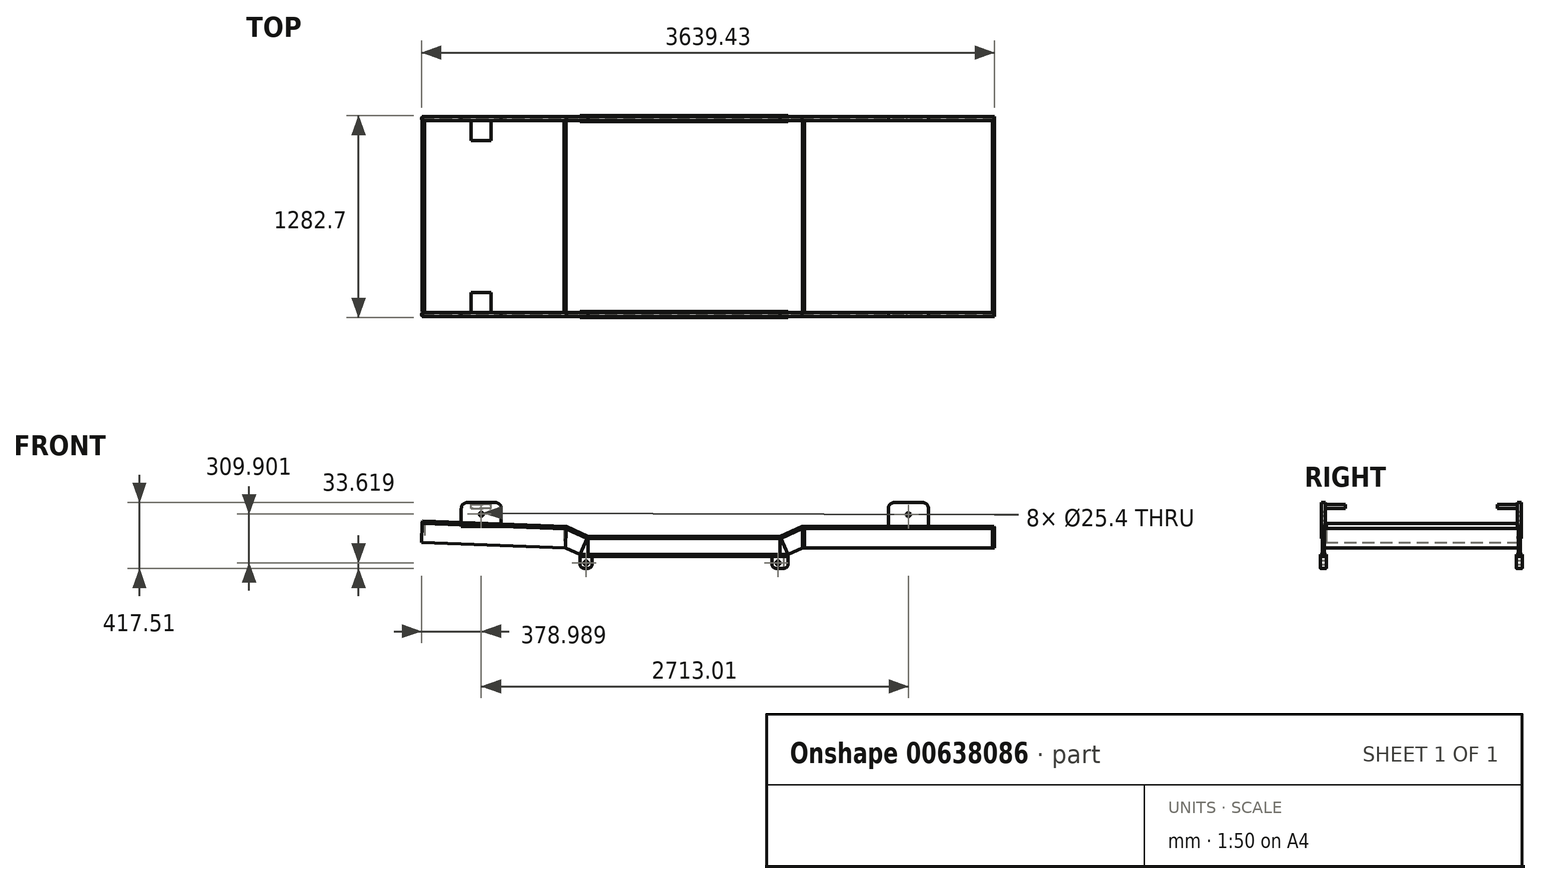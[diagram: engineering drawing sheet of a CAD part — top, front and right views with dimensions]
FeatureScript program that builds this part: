
annotation { "Feature Type Name" : "Feature", "Feature Type Description" : "" }
export const myFeature = defineFeature(function(context is Context, id is Id, definition is map)
    precondition{}
    {
        {
            var Q0;
            Q0=qCreatedBy(makeId("Right.planeOp"),FACE);
            var sketch = newSketch(context, id + "F0", { "sketchPlane" : qUnion([Q0])});
            skLineSegment(sketch, "E0.bottom", {"start": v(-635, 0) * mm, "end": v(-609.6, 0) * mm});
            skLineSegment(sketch, "E0.top", {"start": v(-635, -12.7) * mm, "end": v(-609.6, -12.7) * mm});
            skLineSegment(sketch, "E0.left", {"start": v(-635, 0) * mm, "end": v(-635, -12.7) * mm});
            skLineSegment(sketch, "E0.right", {"start": v(-609.6, 0) * mm, "end": v(-609.6, -12.7) * mm});
            skLineSegment(sketch, "E1.bottom", {"start": v(-628.65, -12.7) * mm, "end": v(-615.95, -12.7) * mm});
            skLineSegment(sketch, "E1.top", {"start": v(-628.65, -114.3) * mm, "end": v(-615.95, -114.3) * mm});
            skLineSegment(sketch, "E1.left", {"start": v(-628.65, -12.7) * mm, "end": v(-628.65, -114.3) * mm});
            skLineSegment(sketch, "E1.right", {"start": v(-615.95, -12.7) * mm, "end": v(-615.95, -114.3) * mm});
            skLineSegment(sketch, "E2.bottom", {"start": v(-641.35, -114.3) * mm, "end": v(-603.25, -114.3) * mm});
            skLineSegment(sketch, "E2.top", {"start": v(-641.35, -127) * mm, "end": v(-603.25, -127) * mm});
            skLineSegment(sketch, "E2.left", {"start": v(-641.35, -114.3) * mm, "end": v(-641.35, -127) * mm});
            skLineSegment(sketch, "E2.right", {"start": v(-603.25, -114.3) * mm, "end": v(-603.25, -127) * mm});
            skLineSegment(sketch, "E3", {"start": v(0, 0) * mm, "end": v(0, -132.95) * mm});
            skLineSegment(sketch, "E4.MirrorCS", {"start": v(635, 0) * mm, "end": v(609.6, 0) * mm});
            skLineSegment(sketch, "E5.MirrorCS", {"start": v(635, 0) * mm, "end": v(635, -12.7) * mm});
            skLineSegment(sketch, "E6.MirrorCS", {"start": v(628.65, -12.7) * mm, "end": v(615.95, -12.7) * mm});
            skLineSegment(sketch, "E7.MirrorCS", {"start": v(635, -12.7) * mm, "end": v(609.6, -12.7) * mm});
            skLineSegment(sketch, "E8.MirrorCS", {"start": v(609.6, 0) * mm, "end": v(609.6, -12.7) * mm});
            skLineSegment(sketch, "E9.MirrorCS", {"start": v(615.95, -12.7) * mm, "end": v(615.95, -114.3) * mm});
            skLineSegment(sketch, "E10.MirrorCS", {"start": v(628.65, -12.7) * mm, "end": v(628.65, -114.3) * mm});
            skLineSegment(sketch, "E11.MirrorCS", {"start": v(641.35, -127) * mm, "end": v(603.25, -127) * mm});
            skLineSegment(sketch, "E12.MirrorCS", {"start": v(603.25, -114.3) * mm, "end": v(603.25, -127) * mm});
            skLineSegment(sketch, "E13.MirrorCS", {"start": v(641.35, -114.3) * mm, "end": v(641.35, -127) * mm});
            skLineSegment(sketch, "E14.MirrorCS", {"start": v(641.35, -114.3) * mm, "end": v(603.25, -114.3) * mm});
            skLineSegment(sketch, "E15", {"start": v(-609.6, -12.7) * mm, "end": v(609.6, -12.7) * mm});
            skLineSegment(sketch, "E16.bottom", {"start": v(615.95, -12.7) * mm, "end": v(628.65, -12.7) * mm});
            skLineSegment(sketch, "E16.top", {"start": v(615.95, -114.3) * mm, "end": v(628.65, -114.3) * mm});
            skSolve(sketch);
        }
        {
            var Q0;
            Q0=makeQuery(id+"F0.imprint","IMPRINT",FACE,{"disambiguationData":[TD([[makeQuery(id+"F0.imprint","IMPRINT",EDGE,{"derivedFrom":sQuery(id+"F0.wireOp",EDGE,"E6.MirrorCS")}),1.0]])]});
            var Q1;
            Q1=makeQuery(id+"F0.imprint","IMPRINT",FACE,{"disambiguationData":[TD([[makeQuery(id+"F0.imprint","IMPRINT",EDGE,{"derivedFrom":sQuery(id+"F0.wireOp",EDGE,"E4.MirrorCS")}),1.0]])]});
            var Q2;
            Q2=makeQuery(id+"F0.imprint","IMPRINT",FACE,{"disambiguationData":[TD([[makeQuery(id+"F0.imprint","IMPRINT",EDGE,{"derivedFrom":sQuery(id+"F0.wireOp",EDGE,"E11.MirrorCS")}),-1.0]])]});
            var Q3;
            Q3=makeQuery(id+"F0.imprint","IMPRINT",FACE,{"disambiguationData":[TD([[makeQuery(id+"F0.imprint","IMPRINT",EDGE,{"derivedFrom":sQuery(id+"F0.wireOp",EDGE,"E1.top")}),1.0]])]});
            var Q4;
            Q4=makeQuery(id+"F0.imprint","IMPRINT",FACE,{"disambiguationData":[TD([[makeQuery(id+"F0.imprint","IMPRINT",EDGE,{"derivedFrom":sQuery(id+"F0.wireOp",EDGE,"E0.bottom")}),-1.0]])]});
            var Q5;
            Q5=makeQuery(id+"F0.imprint","IMPRINT",FACE,{"disambiguationData":[TD([[makeQuery(id+"F0.imprint","IMPRINT",EDGE,{"derivedFrom":sQuery(id+"F0.wireOp",EDGE,"E2.bottom")}),-1.0]])]});
            extrude(context, id + "F1", {"entities" : qUnion([Q0, Q1, Q2, Q3, Q4, Q5]), "depth" : 1219.2 * mm, "offsetDistance" : 25.4 * mm});
        }
        {
            var Q0;
            Q0=makeQuery(id+"F1.opExtrude","CAP_FACE",FACE,{"disambiguationData":[OSD([sQuery(id+"F0.wireOp",EDGE,"E4.MirrorCS"),sQuery(id+"F0.wireOp",EDGE,"E5.MirrorCS"),sQuery(id+"F0.wireOp",EDGE,"E7.MirrorCS"),sQuery(id+"F0.wireOp",EDGE,"E8.MirrorCS"),sQuery(id+"F0.wireOp",EDGE,"E9.MirrorCS"),sQuery(id+"F0.wireOp",EDGE,"E10.MirrorCS"),sQuery(id+"F0.wireOp",EDGE,"E16.top")])],"isStart":true});
            var sketch = newSketch(context, id + "F2", { "sketchPlane" : qUnion([Q0])});
            skLineSegment(sketch, "E17.bottom", {"start": v(-628.65, -12.7) * mm, "end": v(-615.95, -12.7) * mm});
            skLineSegment(sketch, "E17.top", {"start": v(-628.65, -114.3) * mm, "end": v(-615.95, -114.3) * mm});
            skLineSegment(sketch, "E17.left", {"start": v(-628.65, -12.7) * mm, "end": v(-628.65, -114.3) * mm});
            skLineSegment(sketch, "E17.right", {"start": v(-615.95, -12.7) * mm, "end": v(-615.95, -114.3) * mm});
            skLineSegment(sketch, "E18.bottom", {"start": v(-635, 0) * mm, "end": v(-609.6, 0) * mm});
            skLineSegment(sketch, "E18.top", {"start": v(-635, -12.7) * mm, "end": v(-609.6, -12.7) * mm});
            skLineSegment(sketch, "E18.left", {"start": v(-635, 0) * mm, "end": v(-635, -12.7) * mm});
            skLineSegment(sketch, "E18.right", {"start": v(-609.6, 0) * mm, "end": v(-609.6, -12.7) * mm});
            skLineSegment(sketch, "E19.bottom", {"start": v(-641.35, -114.34) * mm, "end": v(-603.26, -114.34) * mm});
            skLineSegment(sketch, "E19.top", {"start": v(-641.35, -127.04) * mm, "end": v(-603.26, -127.04) * mm});
            skLineSegment(sketch, "E19.left", {"start": v(-641.35, -114.34) * mm, "end": v(-641.35, -127.04) * mm});
            skLineSegment(sketch, "E19.right", {"start": v(-603.26, -114.34) * mm, "end": v(-603.26, -127.04) * mm});
            skLineSegment(sketch, "E20", {"start": v(0, 80.16) * mm, "end": v(0, -74.98) * mm});
            skLineSegment(sketch, "E21", {"start": v(0, 80.16) * mm, "end": v(0, -337.85) * mm});
            skLineSegment(sketch, "E22.MirrorCS", {"start": v(635, 0) * mm, "end": v(609.6, 0) * mm});
            skLineSegment(sketch, "E23.MirrorCS", {"start": v(609.6, 0) * mm, "end": v(609.6, -12.7) * mm});
            skLineSegment(sketch, "E24.MirrorCS", {"start": v(635, 0) * mm, "end": v(635, -12.7) * mm});
            skLineSegment(sketch, "E25.MirrorCS", {"start": v(615.95, -12.7) * mm, "end": v(615.95, -114.3) * mm});
            skLineSegment(sketch, "E26.MirrorCS", {"start": v(628.65, -12.7) * mm, "end": v(628.65, -114.3) * mm});
            skLineSegment(sketch, "E27.MirrorCS", {"start": v(603.26, -114.34) * mm, "end": v(603.26, -127.04) * mm});
            skLineSegment(sketch, "E28.MirrorCS", {"start": v(641.35, -127.04) * mm, "end": v(603.26, -127.04) * mm});
            skLineSegment(sketch, "E29.MirrorCS", {"start": v(641.35, -114.34) * mm, "end": v(641.35, -127.04) * mm});
            skSolve(sketch);
        }
        {
            var Q0;
            {var subQ2=sQuery(id+"F2.wireOp",EDGE,"E17.bottom");var subQ6=makeQuery(id+"F2.imprint","IMPRINT",EDGE,{"derivedFrom":subQ2});Q0=qUnion([makeQuery(id+"F2.imprint","IMPRINT",FACE,{"disambiguationData":[TD([[makeQuery(id+"F2.imprint","IMPRINT",EDGE,{"derivedFrom":sQuery(id+"F2.wireOp",EDGE,"E19.bottom")}),-1.0]])]}),makeQuery(id+"F2.imprint","IMPRINT",FACE,{"disambiguationData":[TD([[subQ6,-1.0]])]}),makeQuery(id+"F2.imprint","IMPRINT",FACE,{"disambiguationData":[TD([[subQ6,1.0]])]})]);}
            var Q1;
            Q1=makeQuery(id+"F1.opExtrude","CAP_FACE",FACE,{"disambiguationData":[OSD([sQuery(id+"F0.wireOp",EDGE,"E0.bottom"),sQuery(id+"F0.wireOp",EDGE,"E0.top"),sQuery(id+"F0.wireOp",EDGE,"E0.left"),sQuery(id+"F0.wireOp",EDGE,"E0.right"),sQuery(id+"F0.wireOp",EDGE,"E1.top"),sQuery(id+"F0.wireOp",EDGE,"E1.left"),sQuery(id+"F0.wireOp",EDGE,"E1.right")])],"isStart":true});
            extrude(context, id + "F3", {"entities" : qUnion([Q0, Q1]), "depth" : 50.8 * mm, "offsetDistance" : 25.4 * mm});
        }
        {
            var Q0;
            Q0=makeQuery(id+"F1.opExtrude","CAP_FACE",FACE,{"disambiguationData":[OSD([sQuery(id+"F0.wireOp",EDGE,"E2.bottom"),sQuery(id+"F0.wireOp",EDGE,"E2.top"),sQuery(id+"F0.wireOp",EDGE,"E2.left"),sQuery(id+"F0.wireOp",EDGE,"E2.right")])],"isStart":true});
            extrude(context, id + "F4", {"entities" : qUnion([Q0]), "operationType" : NewBodyOperationType.ADD, "depth" : 50.8 * mm, "offsetDistance" : 25.4 * mm});
        }
        {
            var Q0;
            Q0=makeQuery(id+"F3.opExtrude","CAP_EDGE",EDGE,{"disambiguationData":[OSD([sQuery(id+"F0.wireOp",EDGE,"E0.bottom")])],"isStart":false});
            chamfer(context, id + "F5", {"entities" : qUnion([Q0]), "chamferType" : ChamferType.TWO_OFFSETS, "width1" : 114.3 * mm, "oppositeDirection" : false, "width2" : 50.8 * mm, "tangentPropagation" : true});
        }
        {
            var Q0;
            Q0=makeQuery(id+"F3.opExtrude","CAP_EDGE",EDGE,{"disambiguationData":[OSD([sQuery(id+"F2.wireOp",EDGE,"E18.bottom")])],"isStart":false});
            chamfer(context, id + "F6", {"entities" : qUnion([Q0]), "chamferType" : ChamferType.TWO_OFFSETS, "width1" : 50.8 * mm, "oppositeDirection" : false, "width2" : 114.3 * mm, "tangentPropagation" : true});
        }
        {
            var Q0;
            Q0=makeQuery(id+"F6.opChamfer","BLEND_FACE",FACE,{"disambiguationData":[OSD([sQuery(id+"F2.wireOp",EDGE,"E18.bottom")])]});
            var Q1;
            Q1=makeQuery(id+"F5.opChamfer","BLEND_FACE",FACE,{"disambiguationData":[OSD([sQuery(id+"F0.wireOp",EDGE,"E0.bottom")])]});
            extrude(context, id + "F7", {"entities" : qUnion([Q0, Q1]), "depth" : 152.4 * mm, "offsetDistance" : 25.4 * mm});
        }
        {
            var Q0;
            Q0=makeQuery(id+"F7.opExtrude","CAP_EDGE",EDGE,{"disambiguationData":[OSD([sQuery(id+"F2.wireOp",EDGE,"E17.top"),sQuery(id+"F2.wireOp",EDGE,"E18.bottom")])],"isStart":false});
            chamfer(context, id + "F8", {"entities" : qUnion([Q0]), "chamferType" : ChamferType.TWO_OFFSETS, "width1" : 50.8 * mm, "oppositeDirection" : false, "width2" : 127 * mm, "tangentPropagation" : true});
        }
        {
            var Q0;
            Q0=makeQuery(id+"F7.opExtrude","CAP_EDGE",EDGE,{"disambiguationData":[OSD([sQuery(id+"F0.wireOp",EDGE,"E0.bottom"),sQuery(id+"F0.wireOp",EDGE,"E1.top")])],"isStart":false});
            chamfer(context, id + "F9", {"entities" : qUnion([Q0]), "chamferType" : ChamferType.TWO_OFFSETS, "width1" : 50.8 * mm, "oppositeDirection" : false, "width2" : 127 * mm, "tangentPropagation" : true});
        }
        {
            var Q0;
            Q0=makeQuery(id+"F8.opChamfer","BLEND_FACE",FACE,{"disambiguationData":[OSD([sQuery(id+"F2.wireOp",EDGE,"E17.top"),sQuery(id+"F2.wireOp",EDGE,"E18.bottom")])]});
            var Q1;
            Q1=makeQuery(id+"F9.opChamfer","BLEND_FACE",FACE,{"disambiguationData":[OSD([sQuery(id+"F0.wireOp",EDGE,"E0.bottom"),sQuery(id+"F0.wireOp",EDGE,"E1.top")])]});
            extrude(context, id + "F10", {"entities" : qUnion([Q0, Q1]), "depth" : 914.4 * mm, "offsetDistance" : 25.4 * mm});
        }
        {
            var Q0;
            Q0=makeQuery(id+"F1.opExtrude","CAP_FACE",FACE,{"disambiguationData":[OSD([sQuery(id+"F0.wireOp",EDGE,"E0.bottom"),sQuery(id+"F0.wireOp",EDGE,"E0.top"),sQuery(id+"F0.wireOp",EDGE,"E0.left"),sQuery(id+"F0.wireOp",EDGE,"E0.right"),sQuery(id+"F0.wireOp",EDGE,"E1.top"),sQuery(id+"F0.wireOp",EDGE,"E1.left"),sQuery(id+"F0.wireOp",EDGE,"E1.right")])],"isStart":false});
            var Q1;
            Q1=makeQuery(id+"F1.opExtrude","CAP_FACE",FACE,{"disambiguationData":[OSD([sQuery(id+"F0.wireOp",EDGE,"E2.bottom"),sQuery(id+"F0.wireOp",EDGE,"E2.top"),sQuery(id+"F0.wireOp",EDGE,"E2.left"),sQuery(id+"F0.wireOp",EDGE,"E2.right")])],"isStart":false});
            var Q2;
            Q2=makeQuery(id+"F1.opExtrude","CAP_FACE",FACE,{"disambiguationData":[OSD([sQuery(id+"F0.wireOp",EDGE,"E4.MirrorCS"),sQuery(id+"F0.wireOp",EDGE,"E5.MirrorCS"),sQuery(id+"F0.wireOp",EDGE,"E7.MirrorCS"),sQuery(id+"F0.wireOp",EDGE,"E8.MirrorCS"),sQuery(id+"F0.wireOp",EDGE,"E9.MirrorCS"),sQuery(id+"F0.wireOp",EDGE,"E10.MirrorCS"),sQuery(id+"F0.wireOp",EDGE,"E16.top")])],"isStart":false});
            var Q3;
            Q3=makeQuery(id+"F1.opExtrude","CAP_FACE",FACE,{"disambiguationData":[OSD([sQuery(id+"F0.wireOp",EDGE,"E11.MirrorCS"),sQuery(id+"F0.wireOp",EDGE,"E12.MirrorCS"),sQuery(id+"F0.wireOp",EDGE,"E13.MirrorCS"),sQuery(id+"F0.wireOp",EDGE,"E14.MirrorCS")])],"isStart":false});
            extrude(context, id + "F11", {"entities" : qUnion([Q0, Q1, Q2, Q3]), "depth" : 50.8 * mm, "offsetDistance" : 25.4 * mm});
        }
        {
            var Q0;
            Q0=makeQuery(id+"F11.opExtrude","CAP_EDGE",EDGE,{"disambiguationData":[OSD([sQuery(id+"F0.wireOp",EDGE,"E0.bottom")])],"isStart":false});
            chamfer(context, id + "F12", {"entities" : qUnion([Q0]), "chamferType" : ChamferType.TWO_OFFSETS, "width1" : 50.8 * mm, "oppositeDirection" : false, "width2" : 114.3 * mm, "tangentPropagation" : true});
        }
        {
            var Q0;
            Q0=makeQuery(id+"F11.opExtrude","CAP_EDGE",EDGE,{"disambiguationData":[OSD([sQuery(id+"F0.wireOp",EDGE,"E4.MirrorCS")])],"isStart":false});
            chamfer(context, id + "F13", {"entities" : qUnion([Q0]), "chamferType" : ChamferType.TWO_OFFSETS, "width1" : 114.3 * mm, "oppositeDirection" : false, "width2" : 50.8 * mm, "tangentPropagation" : true});
        }
        {
            var Q0;
            Q0=makeQuery(id+"F12.opChamfer","BLEND_FACE",FACE,{"disambiguationData":[OSD([sQuery(id+"F0.wireOp",EDGE,"E0.bottom")])]});
            var Q1;
            Q1=makeQuery(id+"F13.opChamfer","BLEND_FACE",FACE,{"disambiguationData":[OSD([sQuery(id+"F0.wireOp",EDGE,"E4.MirrorCS")])]});
            extrude(context, id + "F14", {"entities" : qUnion([Q0, Q1]), "depth" : 152.4 * mm, "offsetDistance" : 25.4 * mm});
        }
        {
            var Q0;
            Q0=makeQuery(id+"F14.opExtrude","CAP_EDGE",EDGE,{"disambiguationData":[OSD([sQuery(id+"F0.wireOp",EDGE,"E0.bottom"),sQuery(id+"F0.wireOp",EDGE,"E1.top")])],"isStart":false});
            var Q1;
            Q1=makeQuery(id+"F14.opExtrude","CAP_EDGE",EDGE,{"disambiguationData":[OSD([sQuery(id+"F0.wireOp",EDGE,"E4.MirrorCS"),sQuery(id+"F0.wireOp",EDGE,"E16.top")])],"isStart":false});
            chamfer(context, id + "F15", {"entities" : qUnion([Q0, Q1]), "chamferType" : ChamferType.TWO_OFFSETS, "width1" : 114.3 * mm, "oppositeDirection" : false, "width2" : 50.8 * mm, "tangentPropagation" : true});
        }
        {
            var Q0;
            Q0=makeQuery(id+"F15.opChamfer","BLEND_FACE",FACE,{"disambiguationData":[OSD([sQuery(id+"F0.wireOp",EDGE,"E0.bottom"),sQuery(id+"F0.wireOp",EDGE,"E1.top")])]});
            var Q1;
            Q1=makeQuery(id+"F14.opExtrude","CAP_FACE",FACE,{"disambiguationData":[OSD([sQuery(id+"F0.wireOp",EDGE,"E0.bottom")])],"isStart":false});
            var Q2;
            Q2=makeQuery(id+"F14.opExtrude","CAP_FACE",FACE,{"disambiguationData":[OSD([sQuery(id+"F0.wireOp",EDGE,"E4.MirrorCS")])],"isStart":false});
            var Q3;
            Q3=makeQuery(id+"F15.opChamfer","BLEND_FACE",FACE,{"disambiguationData":[OSD([sQuery(id+"F0.wireOp",EDGE,"E4.MirrorCS"),sQuery(id+"F0.wireOp",EDGE,"E16.top")])]});
            extrude(context, id + "F16", {"entities" : qUnion([Q0, Q1, Q2, Q3]), "depth" : 1219.2 * mm, "offsetDistance" : 25.4 * mm});
        }
        {
            var Q0;
            Q0=makeQuery(id+"F16.opExtrude","SWEPT_FACE",FACE,{"disambiguationData":[OSD([sQuery(id+"F0.wireOp",EDGE,"E4.MirrorCS"),sQuery(id+"F0.wireOp",EDGE,"E9.MirrorCS"),sQuery(id+"F0.wireOp",EDGE,"E16.top")])]});
            var sketch = newSketch(context, id + "F17", { "sketchPlane" : qUnion([Q0])});
            skLineSegment(sketch, "E30.bottom", {"start": v(2582.04, 48.63) * mm, "end": v(2569.34, 48.63) * mm});
            skLineSegment(sketch, "E30.top", {"start": v(2582.04, -73.04) * mm, "end": v(2569.34, -73.04) * mm});
            skLineSegment(sketch, "E30.left", {"start": v(2582.04, 48.63) * mm, "end": v(2582.04, -73.04) * mm});
            skLineSegment(sketch, "E30.right", {"start": v(2569.34, 48.63) * mm, "end": v(2569.34, -73.04) * mm});
            skLineSegment(sketch, "E31.bottom", {"start": v(1362.84, 48.63) * mm, "end": v(1375.54, 48.63) * mm});
            skLineSegment(sketch, "E31.top", {"start": v(1362.84, -73.04) * mm, "end": v(1375.54, -73.04) * mm});
            skLineSegment(sketch, "E31.left", {"start": v(1362.84, 48.63) * mm, "end": v(1362.84, -73.04) * mm});
            skLineSegment(sketch, "E31.right", {"start": v(1375.54, 48.63) * mm, "end": v(1375.54, -73.04) * mm});
            skSolve(sketch);
        }
        {
            var Q0;
            Q0=makeQuery(id+"F17.imprint","IMPRINT",FACE,{"disambiguationData":[TD([[makeQuery(id+"F17.imprint","IMPRINT",EDGE,{"derivedFrom":sQuery(id+"F17.wireOp",EDGE,"E31.bottom")}),1.0]])]});
            var Q1;
            Q1=makeQuery(id+"F17.imprint","IMPRINT",FACE,{"disambiguationData":[TD([[makeQuery(id+"F17.imprint","IMPRINT",EDGE,{"derivedFrom":sQuery(id+"F17.wireOp",EDGE,"E30.bottom")}),1.0]])]});
            extrude(context, id + "F18", {"entities" : qUnion([Q0, Q1]), "depth" : 1244.6 * mm, "offsetDistance" : 25.4 * mm});
        }
        {
            var Q0;
            Q0=makeQuery(id+"F10.opExtrude","SWEPT_FACE",FACE,{"disambiguationData":[OSD([sQuery(id+"F2.wireOp",EDGE,"E17.top"),sQuery(id+"F2.wireOp",EDGE,"E17.right"),sQuery(id+"F2.wireOp",EDGE,"E18.bottom")])]});
            var sketch = newSketch(context, id + "F19", { "sketchPlane" : qUnion([Q0])});
            skLineSegment(sketch, "E32.bottom", {"start": v(-1052.88, 81.1) * mm, "end": v(-1040.18, 81.1) * mm});
            skLineSegment(sketch, "E32.top", {"start": v(-1052.88, -39.2) * mm, "end": v(-1040.18, -39.2) * mm});
            skLineSegment(sketch, "E32.left", {"start": v(-1052.88, 81.1) * mm, "end": v(-1052.88, -39.2) * mm});
            skLineSegment(sketch, "E32.right", {"start": v(-1040.18, 81.1) * mm, "end": v(-1040.18, -39.2) * mm});
            skLineSegment(sketch, "E33.bottom", {"start": v(-139.13, 46.63) * mm, "end": v(-151.83, 46.63) * mm});
            skLineSegment(sketch, "E33.top", {"start": v(-139.13, -72.73) * mm, "end": v(-151.83, -72.73) * mm});
            skLineSegment(sketch, "E33.left", {"start": v(-139.13, 46.63) * mm, "end": v(-139.13, -72.73) * mm});
            skLineSegment(sketch, "E33.right", {"start": v(-151.83, 46.63) * mm, "end": v(-151.83, -72.73) * mm});
            skSolve(sketch);
        }
        {
            var Q0;
            {var subQ1=sQuery(id+"F2.wireOp",EDGE,"E18.bottom");var subQ2=sQuery(id+"F2.wireOp",EDGE,"E17.right");var subQ3=sQuery(id+"F2.wireOp",EDGE,"E17.top");var subQ6=makeQuery(id+"F10.opExtrude","SWEPT_EDGE",EDGE,{"disambiguationData":[OSD([subQ3,subQ2,subQ1])]});var subQ8=sQuery(id+"F19.wireOp",EDGE,"E32.right");var subQ10=makeQuery(id+"F19.imprint","INTERSECT",VERTEX,{"derivedFrom":[subQ6,sQuery(id+"F19.wireOp",EDGE,"E32.top"),subQ8]});Q0=makeQuery(id+"F19.imprint","IMPRINT",FACE,{"disambiguationData":[TD([[makeQuery(id+"F19.imprint","IMPRINT",EDGE,{"disambiguationData":[TD([[subQ10,1.0]])],"derivedFrom":subQ8}),-1.0]])]});}
            var Q1;
            {var subQ0=sQuery(id+"F19.wireOp",EDGE,"E33.left");Q1=makeQuery(id+"F19.imprint","IMPRINT",FACE,{"disambiguationData":[TD([[makeQuery(id+"F19.imprint","IMPRINT",EDGE,{"derivedFrom":subQ0}),-1.0]])]});}
            var Q2;
            {var subQ0=sQuery(id+"F19.wireOp",EDGE,"E33.bottom");Q2=makeQuery(id+"F19.imprint","IMPRINT",FACE,{"disambiguationData":[TD([[makeQuery(id+"F19.imprint","IMPRINT",EDGE,{"derivedFrom":subQ0}),1.0]])]});}
            extrude(context, id + "F20", {"entities" : qUnion([Q0, Q1, Q2]), "depth" : 1219.2 * mm, "offsetDistance" : 25.4 * mm});
        }
        {
            var Q0;
            Q0=makeQuery(id+"F16.opExtrude","SWEPT_FACE",FACE,{"disambiguationData":[OSD([sQuery(id+"F0.wireOp",EDGE,"E0.bottom"),sQuery(id+"F0.wireOp",EDGE,"E0.top"),sQuery(id+"F0.wireOp",EDGE,"E0.left"),sQuery(id+"F0.wireOp",EDGE,"E0.right"),sQuery(id+"F0.wireOp",EDGE,"E1.top"),sQuery(id+"F0.wireOp",EDGE,"E1.left"),sQuery(id+"F0.wireOp",EDGE,"E1.right")])]});
            var sketch = newSketch(context, id + "F21", { "sketchPlane" : qUnion([Q0])});
            skLineSegment(sketch, "E34.bottom", {"start": v(1907.61, -609.6) * mm, "end": v(2161.61, -609.6) * mm});
            skLineSegment(sketch, "E34.top", {"start": v(1907.61, -635) * mm, "end": v(2161.61, -635) * mm});
            skLineSegment(sketch, "E34.left", {"start": v(1907.61, -609.6) * mm, "end": v(1907.61, -635) * mm});
            skLineSegment(sketch, "E34.right", {"start": v(2161.61, -609.6) * mm, "end": v(2161.61, -635) * mm});
            skLineSegment(sketch, "E35", {"start": v(0, 0) * mm, "end": v(2582.14, 0) * mm});
            skLineSegment(sketch, "E36.MirrorCS", {"start": v(1907.61, 609.6) * mm, "end": v(2161.61, 609.6) * mm});
            skLineSegment(sketch, "E37.MirrorCS", {"start": v(2161.61, 609.6) * mm, "end": v(2161.61, 635) * mm});
            skLineSegment(sketch, "E38.MirrorCS", {"start": v(1907.61, 609.6) * mm, "end": v(1907.61, 635) * mm});
            skLineSegment(sketch, "E39.MirrorCS", {"start": v(1907.61, 635) * mm, "end": v(2161.61, 635) * mm});
            skLineSegment(sketch, "E40", {"start": v(678.1, 638.57) * mm, "end": v(678.1, -643.37) * mm});
            skLineSegment(sketch, "E41.MirrorCS", {"start": v(-551.4, -609.6) * mm, "end": v(-805.4, -609.6) * mm});
            skLineSegment(sketch, "E42.MirrorCS", {"start": v(-551.4, -609.6) * mm, "end": v(-551.4, -635) * mm});
            skLineSegment(sketch, "E43.MirrorCS", {"start": v(-551.4, -635) * mm, "end": v(-805.4, -635) * mm});
            skLineSegment(sketch, "E44.MirrorCS", {"start": v(-805.4, -609.6) * mm, "end": v(-805.4, -635) * mm});
            skLineSegment(sketch, "E45.MirrorCS", {"start": v(-551.4, 635) * mm, "end": v(-805.4, 635) * mm});
            skLineSegment(sketch, "E46.MirrorCS", {"start": v(-551.4, 609.6) * mm, "end": v(-805.4, 609.6) * mm});
            skLineSegment(sketch, "E47.MirrorCS", {"start": v(-551.4, 609.6) * mm, "end": v(-551.4, 635) * mm});
            skLineSegment(sketch, "E48.MirrorCS", {"start": v(-805.4, 609.6) * mm, "end": v(-805.4, 635) * mm});
            skSolve(sketch);
        }
        {
            var Q0;
            Q0 = qSketchRegion(id + "F21", true);
            extrude(context, id + "F22", {"entities" : qUnion([Q0]), "depth" : 152.4 * mm, "offsetDistance" : 25.4 * mm});
        }
        {
            var Q0;
            Q0=makeQuery(id+"F22.opExtrude","CAP_EDGE",EDGE,{"disambiguationData":[OSD([sQuery(id+"F21.wireOp",EDGE,"E37.MirrorCS")])],"isStart":false});
            var Q1;
            Q1=makeQuery(id+"F22.opExtrude","CAP_EDGE",EDGE,{"disambiguationData":[OSD([sQuery(id+"F21.wireOp",EDGE,"E34.right")])],"isStart":false});
            var Q2;
            Q2=makeQuery(id+"F22.opExtrude","CAP_EDGE",EDGE,{"disambiguationData":[OSD([sQuery(id+"F21.wireOp",EDGE,"E42.MirrorCS")])],"isStart":false});
            var Q3;
            Q3=makeQuery(id+"F22.opExtrude","CAP_EDGE",EDGE,{"disambiguationData":[OSD([sQuery(id+"F21.wireOp",EDGE,"E47.MirrorCS")])],"isStart":false});
            var Q4;
            Q4=makeQuery(id+"F22.opExtrude","CAP_EDGE",EDGE,{"disambiguationData":[OSD([sQuery(id+"F21.wireOp",EDGE,"E38.MirrorCS")])],"isStart":false});
            var Q5;
            Q5=makeQuery(id+"F22.opExtrude","CAP_EDGE",EDGE,{"disambiguationData":[OSD([sQuery(id+"F21.wireOp",EDGE,"E44.MirrorCS")])],"isStart":false});
            var Q6;
            Q6=makeQuery(id+"F22.opExtrude","CAP_EDGE",EDGE,{"disambiguationData":[OSD([sQuery(id+"F21.wireOp",EDGE,"E48.MirrorCS")])],"isStart":false});
            var Q7;
            Q7=makeQuery(id+"F22.opExtrude","CAP_EDGE",EDGE,{"disambiguationData":[OSD([sQuery(id+"F21.wireOp",EDGE,"E34.left")])],"isStart":false});
            fillet(context, id + "F23", {"entities" : qUnion([Q0, Q1, Q2, Q3, Q4, Q5, Q6, Q7]), "radius" : 38.1 * mm, "tangentPropagation" : true, "allowEdgeOverflow" : false});
        }
        {
            var Q0;
            Q0=makeQuery(id+"F22.opExtrude","SWEPT_FACE",FACE,{"disambiguationData":[OSD([sQuery(id+"F21.wireOp",EDGE,"E43.MirrorCS")])]});
            var sketch = newSketch(context, id + "F24", { "sketchPlane" : qUnion([Q0])});
            skPoint(sketch, "E49", {"position": v(-678.4, 140.3) * mm});
            skPoint(sketch, "E50", {"position": v(2034.61, 137.03) * mm});
            skSolve(sketch);
        }
        {
            var Q0;
            Q0=sQuery(id+"F24.wireOp",VERTEX,"E50");
            var Q1;
            Q1=sQuery(id+"F24.wireOp",VERTEX,"E49");
            var Q2;
            Q2=makeQuery(id+"F22.opExtrude","SWEPT_BODY",BODY,{"disambiguationData":[OSD([sQuery(id+"F21.wireOp",EDGE,"E34.bottom"),sQuery(id+"F21.wireOp",EDGE,"E34.top"),sQuery(id+"F21.wireOp",EDGE,"E34.left"),sQuery(id+"F21.wireOp",EDGE,"E34.right")])]});
            var Q3;
            Q3=makeQuery(id+"F22.opExtrude","SWEPT_BODY",BODY,{"disambiguationData":[OSD([sQuery(id+"F21.wireOp",EDGE,"E36.MirrorCS"),sQuery(id+"F21.wireOp",EDGE,"E37.MirrorCS"),sQuery(id+"F21.wireOp",EDGE,"E38.MirrorCS"),sQuery(id+"F21.wireOp",EDGE,"E39.MirrorCS")])]});
            var Q4;
            Q4=makeQuery(id+"F22.opExtrude","SWEPT_BODY",BODY,{"disambiguationData":[OSD([sQuery(id+"F21.wireOp",EDGE,"E41.MirrorCS"),sQuery(id+"F21.wireOp",EDGE,"E42.MirrorCS"),sQuery(id+"F21.wireOp",EDGE,"E43.MirrorCS"),sQuery(id+"F21.wireOp",EDGE,"E44.MirrorCS")])]});
            var Q5;
            Q5=makeQuery(id+"F22.opExtrude","SWEPT_BODY",BODY,{"disambiguationData":[OSD([sQuery(id+"F21.wireOp",EDGE,"E45.MirrorCS"),sQuery(id+"F21.wireOp",EDGE,"E46.MirrorCS"),sQuery(id+"F21.wireOp",EDGE,"E47.MirrorCS"),sQuery(id+"F21.wireOp",EDGE,"E48.MirrorCS")])]});
            hole(context, id + "F25", {"style" : HoleStyle.SIMPLE, "endStyle" : HoleEndStyle.THROUGH, "holeDiameter" : 25.4 * mm, "majorDiameter" : 6.35 * mm, "isTappedThrough" : true, "tappedDepth" : 12.7 * mm, "tapClearance" : 3, "locations" : qUnion([Q0, Q1]), "scope" : qUnion([Q2, Q3, Q4, Q5])});
        }
        {
            var Q0;
            Q0=makeQuery(id+"F22.opExtrude","SWEPT_FACE",FACE,{"disambiguationData":[OSD([sQuery(id+"F21.wireOp",EDGE,"E46.MirrorCS")])]});
            var sketch = newSketch(context, id + "F26", { "sketchPlane" : qUnion([Q0])});
            skLineSegment(sketch, "E51.bottom", {"start": v(-615.4, 175.45) * mm, "end": v(-742.4, 175.45) * mm});
            skLineSegment(sketch, "E51.top", {"start": v(-615.4, 200.85) * mm, "end": v(-742.4, 200.85) * mm});
            skLineSegment(sketch, "E51.left", {"start": v(-615.4, 175.45) * mm, "end": v(-615.4, 200.85) * mm});
            skLineSegment(sketch, "E51.right", {"start": v(-742.4, 175.45) * mm, "end": v(-742.4, 200.85) * mm});
            skPoint(sketch, "E51.middle", {"position": v(-678.9, 188.15) * mm});
            skSolve(sketch);
        }
        {
            var Q0;
            Q0=makeQuery(id+"F22.opExtrude","SWEPT_FACE",FACE,{"disambiguationData":[OSD([sQuery(id+"F21.wireOp",EDGE,"E41.MirrorCS")])]});
            var sketch = newSketch(context, id + "F27", { "sketchPlane" : qUnion([Q0])});
            skLineSegment(sketch, "E52.bottom", {"start": v(742.35, 175.63) * mm, "end": v(615.35, 175.63) * mm});
            skLineSegment(sketch, "E52.top", {"start": v(742.35, 201.03) * mm, "end": v(615.35, 201.03) * mm});
            skLineSegment(sketch, "E52.left", {"start": v(742.35, 175.63) * mm, "end": v(742.35, 201.03) * mm});
            skLineSegment(sketch, "E52.right", {"start": v(615.35, 175.63) * mm, "end": v(615.35, 201.03) * mm});
            skPoint(sketch, "E52.middle", {"position": v(678.85, 188.33) * mm});
            skSolve(sketch);
        }
        {
            var Q0;
            Q0 = qSketchRegion(id + "F27", true);
            extrude(context, id + "F28", {"entities" : qUnion([Q0]), "operationType" : NewBodyOperationType.ADD, "depth" : 127 * mm, "offsetDistance" : 25.4 * mm});
        }
        {
            var Q0;
            Q0 = qSketchRegion(id + "F26", true);
            extrude(context, id + "F29", {"entities" : qUnion([Q0]), "operationType" : NewBodyOperationType.ADD, "depth" : 127 * mm, "offsetDistance" : 25.4 * mm});
        }
        {
            var Q0;
            {var subQ0=sQuery(id+"F0.wireOp",EDGE,"E2.top");Q0=makeQuery(id+"F4.boolean.opBoolean","MERGE",FACE,{"derivedFrom":[makeQuery(id+"F1.opExtrude","SWEPT_FACE",FACE,{"disambiguationData":[OSD([subQ0])]}),makeQuery(id+"F4.opExtrude","SWEPT_FACE",FACE,{"disambiguationData":[OSD([subQ0])]})]});}
            var sketch = newSketch(context, id + "F30", { "sketchPlane" : qUnion([Q0])});
            skLineSegment(sketch, "E53.bottom", {"start": v(1269.91, 641.27) * mm, "end": v(1244.51, 641.27) * mm});
            skLineSegment(sketch, "E53.top", {"start": v(1269.91, 603.17) * mm, "end": v(1244.51, 603.17) * mm});
            skLineSegment(sketch, "E53.left", {"start": v(1269.91, 641.27) * mm, "end": v(1269.91, 603.17) * mm});
            skLineSegment(sketch, "E53.right", {"start": v(1244.51, 641.27) * mm, "end": v(1244.51, 603.17) * mm});
            skLineSegment(sketch, "E54", {"start": v(0, 0) * mm, "end": v(3179.36, 0) * mm});
            skLineSegment(sketch, "E55.MirrorCS", {"start": v(1269.91, -641.27) * mm, "end": v(1244.51, -641.27) * mm});
            skLineSegment(sketch, "E56.MirrorCS", {"start": v(1269.91, -641.27) * mm, "end": v(1269.91, -603.17) * mm});
            skLineSegment(sketch, "E57.MirrorCS", {"start": v(1244.51, -641.27) * mm, "end": v(1244.51, -603.17) * mm});
            skLineSegment(sketch, "E58.MirrorCS", {"start": v(1269.91, -603.17) * mm, "end": v(1244.51, -603.17) * mm});
            skLineSegment(sketch, "E59.bottom", {"start": v(-50.8, 641.35) * mm, "end": v(-25.4, 641.35) * mm});
            skLineSegment(sketch, "E59.top", {"start": v(-50.8, 603.25) * mm, "end": v(-25.4, 603.25) * mm});
            skLineSegment(sketch, "E59.left", {"start": v(-50.8, 641.35) * mm, "end": v(-50.8, 603.25) * mm});
            skLineSegment(sketch, "E59.right", {"start": v(-25.4, 641.35) * mm, "end": v(-25.4, 603.25) * mm});
            skLineSegment(sketch, "E60", {"start": v(0, 0) * mm, "end": v(-607.31, 0) * mm});
            skLineSegment(sketch, "E61", {"start": v(-607.31, 0) * mm, "end": v(2675.06, 0) * mm});
            skLineSegment(sketch, "E62.MirrorCS", {"start": v(-50.8, -641.35) * mm, "end": v(-50.8, -603.25) * mm});
            skLineSegment(sketch, "E63.MirrorCS", {"start": v(-50.8, -641.35) * mm, "end": v(-25.4, -641.35) * mm});
            skLineSegment(sketch, "E64.MirrorCS", {"start": v(-25.4, -641.35) * mm, "end": v(-25.4, -603.25) * mm});
            skLineSegment(sketch, "E65.MirrorCS", {"start": v(-50.8, -603.25) * mm, "end": v(-25.4, -603.25) * mm});
            skLineSegment(sketch, "E66.bottom", {"start": v(1269.91, 641.27) * mm, "end": v(1168.31, 641.27) * mm});
            skLineSegment(sketch, "E66.top", {"start": v(1269.91, 603.25) * mm, "end": v(1168.31, 603.25) * mm});
            skLineSegment(sketch, "E66.left", {"start": v(1269.91, 641.27) * mm, "end": v(1269.91, 603.25) * mm});
            skLineSegment(sketch, "E66.right", {"start": v(1168.31, 641.27) * mm, "end": v(1168.31, 603.25) * mm});
            skLineSegment(sketch, "E67.MirrorCS", {"start": v(1269.91, -603.25) * mm, "end": v(1168.31, -603.25) * mm});
            skLineSegment(sketch, "E68.MirrorCS", {"start": v(1269.91, -641.27) * mm, "end": v(1168.31, -641.27) * mm});
            skLineSegment(sketch, "E69.MirrorCS", {"start": v(1269.91, -641.27) * mm, "end": v(1269.91, -603.25) * mm});
            skLineSegment(sketch, "E70.MirrorCS", {"start": v(1168.31, -641.27) * mm, "end": v(1168.31, -603.25) * mm});
            skLineSegment(sketch, "E71.bottom", {"start": v(-50.8, 641.35) * mm, "end": v(25.4, 641.35) * mm});
            skLineSegment(sketch, "E71.top", {"start": v(-50.8, 603.25) * mm, "end": v(25.4, 603.25) * mm});
            skLineSegment(sketch, "E71.right", {"start": v(25.4, 641.35) * mm, "end": v(25.4, 603.25) * mm});
            skLineSegment(sketch, "E72.MirrorCS", {"start": v(-50.8, -641.35) * mm, "end": v(25.4, -641.35) * mm});
            skLineSegment(sketch, "E73.MirrorCS", {"start": v(25.4, -641.35) * mm, "end": v(25.4, -603.25) * mm});
            skLineSegment(sketch, "E74.MirrorCS", {"start": v(-50.8, -603.25) * mm, "end": v(25.4, -603.25) * mm});
            skSolve(sketch);
        }
        {
            var Q0;
            {var subQ0=makeQuery(id+"F30.imprint","IMPRINT",EDGE,{"derivedFrom":sQuery(id+"F30.wireOp",EDGE,"E64.MirrorCS")});var subQ1=sQuery(id+"F30.wireOp",EDGE,"E55.MirrorCS");var subQ8=sQuery(id+"F30.wireOp",EDGE,"E68.MirrorCS");var subQ11=sQuery(id+"F30.wireOp",EDGE,"E58.MirrorCS");var subQ12=sQuery(id+"F30.wireOp",EDGE,"E66.right");var subQ14=sQuery(id+"F0.wireOp",EDGE,"E2.top");var subQ15=makeQuery(id+"F1.opExtrude","CAP_EDGE",EDGE,{"disambiguationData":[OSD([subQ14])],"isStart":false});var subQ17=sQuery(id+"F30.wireOp",EDGE,"E66.top");var subQ18=makeQuery(id+"F30.imprint","INTERSECT",VERTEX,{"derivedFrom":[subQ15,subQ17]});var subQ22=sQuery(id+"F30.wireOp",EDGE,"E53.bottom");var subQ26=makeQuery(id+"F30.imprint","IMPRINT",EDGE,{"derivedFrom":sQuery(id+"F30.wireOp",EDGE,"E59.right")});var subQ30=sQuery(id+"F30.wireOp",EDGE,"E53.top");Q0=qUnion([makeQuery(id+"F30.imprint","IMPRINT",FACE,{"disambiguationData":[TD([[makeQuery(id+"F30.imprint","IMPRINT",EDGE,{"derivedFrom":subQ30}),-1.0]])]}),makeQuery(id+"F30.imprint","IMPRINT",FACE,{"disambiguationData":[TD([[makeQuery(id+"F30.imprint","IMPRINT",EDGE,{"derivedFrom":sQuery(id+"F30.wireOp",EDGE,"E59.bottom")}),1.0]])]}),makeQuery(id+"F30.imprint","IMPRINT",FACE,{"disambiguationData":[TD([[makeQuery(id+"F30.imprint","IMPRINT",EDGE,{"derivedFrom":subQ22}),1.0]])]}),makeQuery(id+"F30.imprint","IMPRINT",FACE,{"disambiguationData":[TD([[subQ26,1.0]])]}),makeQuery(id+"F30.imprint","IMPRINT",FACE,{"disambiguationData":[TD([[makeQuery(id+"F30.imprint","IMPRINT",EDGE,{"disambiguationData":[TD([[subQ18,1.0]])],"derivedFrom":subQ17}),-1.0]])]}),makeQuery(id+"F30.imprint","IMPRINT",FACE,{"disambiguationData":[TD([[makeQuery(id+"F30.imprint","IMPRINT",EDGE,{"derivedFrom":subQ12}),1.0]])]}),makeQuery(id+"F30.imprint","IMPRINT",FACE,{"disambiguationData":[TD([[makeQuery(id+"F30.imprint","IMPRINT",EDGE,{"derivedFrom":subQ11}),1.0]])]}),makeQuery(id+"F30.imprint","IMPRINT",FACE,{"disambiguationData":[TD([[makeQuery(id+"F30.imprint","IMPRINT",EDGE,{"derivedFrom":subQ8}),-1.0]])]}),makeQuery(id+"F30.imprint","IMPRINT",FACE,{"disambiguationData":[TD([[makeQuery(id+"F30.imprint","IMPRINT",EDGE,{"derivedFrom":subQ1}),-1.0]])]}),makeQuery(id+"F30.imprint","IMPRINT",FACE,{"disambiguationData":[TD([[makeQuery(id+"F30.imprint","IMPRINT",EDGE,{"derivedFrom":sQuery(id+"F30.wireOp",EDGE,"E62.MirrorCS")}),-1.0]])]}),makeQuery(id+"F30.imprint","IMPRINT",FACE,{"disambiguationData":[TD([[subQ0,-1.0]])]})]);}
            extrude(context, id + "F31", {"entities" : qUnion([Q0]), "depth" : 76.2 * mm, "offsetDistance" : 25.4 * mm});
        }
        {
            var Q0;
            Q0=makeQuery(id+"F31.opExtrude","SWEPT_FACE",FACE,{"disambiguationData":[OSD([sQuery(id+"F30.wireOp",EDGE,"E53.bottom"),sQuery(id+"F30.wireOp",EDGE,"E66.bottom")])]});
            var sketch = newSketch(context, id + "F32", { "sketchPlane" : qUnion([Q0])});
            skPoint(sketch, "E75", {"position": v(1206.41, -169.2) * mm});
            skSolve(sketch);
        }
        {
            var Q0;
            Q0=sQuery(id+"F32.wireOp",VERTEX,"E75");
            var Q1;
            Q1=makeQuery(id+"F31.opExtrude","SWEPT_BODY",BODY,{"disambiguationData":[OSD([sQuery(id+"F30.wireOp",EDGE,"E53.bottom"),sQuery(id+"F30.wireOp",EDGE,"E53.top"),sQuery(id+"F30.wireOp",EDGE,"E53.left"),sQuery(id+"F30.wireOp",EDGE,"E53.right"),sQuery(id+"F30.wireOp",EDGE,"E66.bottom"),sQuery(id+"F30.wireOp",EDGE,"E66.top"),sQuery(id+"F30.wireOp",EDGE,"E66.right")])]});
            var Q2;
            Q2=makeQuery(id+"F31.opExtrude","SWEPT_BODY",BODY,{"disambiguationData":[OSD([sQuery(id+"F30.wireOp",EDGE,"E55.MirrorCS"),sQuery(id+"F30.wireOp",EDGE,"E56.MirrorCS"),sQuery(id+"F30.wireOp",EDGE,"E57.MirrorCS"),sQuery(id+"F30.wireOp",EDGE,"E58.MirrorCS"),sQuery(id+"F30.wireOp",EDGE,"E67.MirrorCS"),sQuery(id+"F30.wireOp",EDGE,"E68.MirrorCS"),sQuery(id+"F30.wireOp",EDGE,"E70.MirrorCS")])]});
            hole(context, id + "F33", {"style" : HoleStyle.SIMPLE, "endStyle" : HoleEndStyle.THROUGH, "holeDiameter" : 25.4 * mm, "majorDiameter" : 6.35 * mm, "isTappedThrough" : true, "tappedDepth" : 12.7 * mm, "tapClearance" : 3, "locations" : qUnion([Q0]), "scope" : qUnion([Q1, Q2])});
        }
        {
            var Q0;
            Q0=makeQuery(id+"F31.opExtrude","SWEPT_FACE",FACE,{"disambiguationData":[OSD([sQuery(id+"F30.wireOp",EDGE,"E59.bottom"),sQuery(id+"F30.wireOp",EDGE,"E71.bottom")])]});
            var sketch = newSketch(context, id + "F34", { "sketchPlane" : qUnion([Q0])});
            skPoint(sketch, "E76", {"position": v(-12.7, -169.6) * mm});
            skSolve(sketch);
        }
        {
            var Q0;
            Q0=sQuery(id+"F34.wireOp",VERTEX,"E76");
            var Q1;
            Q1=makeQuery(id+"F31.opExtrude","SWEPT_BODY",BODY,{"disambiguationData":[OSD([sQuery(id+"F30.wireOp",EDGE,"E59.bottom"),sQuery(id+"F30.wireOp",EDGE,"E59.top"),sQuery(id+"F30.wireOp",EDGE,"E59.left"),sQuery(id+"F30.wireOp",EDGE,"E71.bottom"),sQuery(id+"F30.wireOp",EDGE,"E71.top"),sQuery(id+"F30.wireOp",EDGE,"E71.right")])]});
            var Q2;
            Q2=makeQuery(id+"F31.opExtrude","SWEPT_BODY",BODY,{"disambiguationData":[OSD([sQuery(id+"F30.wireOp",EDGE,"E62.MirrorCS"),sQuery(id+"F30.wireOp",EDGE,"E63.MirrorCS"),sQuery(id+"F30.wireOp",EDGE,"E65.MirrorCS"),sQuery(id+"F30.wireOp",EDGE,"E72.MirrorCS"),sQuery(id+"F30.wireOp",EDGE,"E73.MirrorCS"),sQuery(id+"F30.wireOp",EDGE,"E74.MirrorCS")])]});
            hole(context, id + "F35", {"style" : HoleStyle.SIMPLE, "endStyle" : HoleEndStyle.THROUGH, "holeDiameter" : 25.4 * mm, "majorDiameter" : 6.35 * mm, "isTappedThrough" : true, "tappedDepth" : 12.7 * mm, "tapClearance" : 3, "locations" : qUnion([Q0]), "scope" : qUnion([Q1, Q2])});
        }
        {
            var Q0;
            Q0=makeQuery(id+"F31.opExtrude","CAP_EDGE",EDGE,{"disambiguationData":[OSD([sQuery(id+"F30.wireOp",EDGE,"E53.left")])],"isStart":false});
            var Q1;
            Q1=makeQuery(id+"F31.opExtrude","CAP_EDGE",EDGE,{"disambiguationData":[OSD([sQuery(id+"F30.wireOp",EDGE,"E56.MirrorCS")])],"isStart":false});
            var Q2;
            Q2=makeQuery(id+"F31.opExtrude","CAP_EDGE",EDGE,{"disambiguationData":[OSD([sQuery(id+"F30.wireOp",EDGE,"E70.MirrorCS")])],"isStart":false});
            var Q3;
            Q3=makeQuery(id+"F31.opExtrude","CAP_EDGE",EDGE,{"disambiguationData":[OSD([sQuery(id+"F30.wireOp",EDGE,"E66.right")])],"isStart":false});
            fillet(context, id + "F36", {"entities" : qUnion([Q0, Q1, Q2, Q3]), "tangentPropagation" : true, "radius" : 25.4 * mm, "defaultsChanged" : false, "vertexSettings" : [], "allowEdgeOverflow" : false});
        }
        {
            var Q0;
            Q0=makeQuery(id+"F31.opExtrude","CAP_EDGE",EDGE,{"disambiguationData":[OSD([sQuery(id+"F30.wireOp",EDGE,"E59.left")])],"isStart":false});
            var Q1;
            Q1=makeQuery(id+"F31.opExtrude","CAP_EDGE",EDGE,{"disambiguationData":[OSD([sQuery(id+"F30.wireOp",EDGE,"E71.right")])],"isStart":false});
            var Q2;
            Q2=makeQuery(id+"F31.opExtrude","CAP_EDGE",EDGE,{"disambiguationData":[OSD([sQuery(id+"F30.wireOp",EDGE,"E73.MirrorCS")])],"isStart":false});
            var Q3;
            Q3=makeQuery(id+"F31.opExtrude","CAP_EDGE",EDGE,{"disambiguationData":[OSD([sQuery(id+"F30.wireOp",EDGE,"E62.MirrorCS")])],"isStart":false});
            fillet(context, id + "F37", {"entities" : qUnion([Q0, Q1, Q2, Q3]), "tangentPropagation" : true, "radius" : 25.4 * mm, "defaultsChanged" : false, "vertexSettings" : [], "allowEdgeOverflow" : false});
        }
    });
